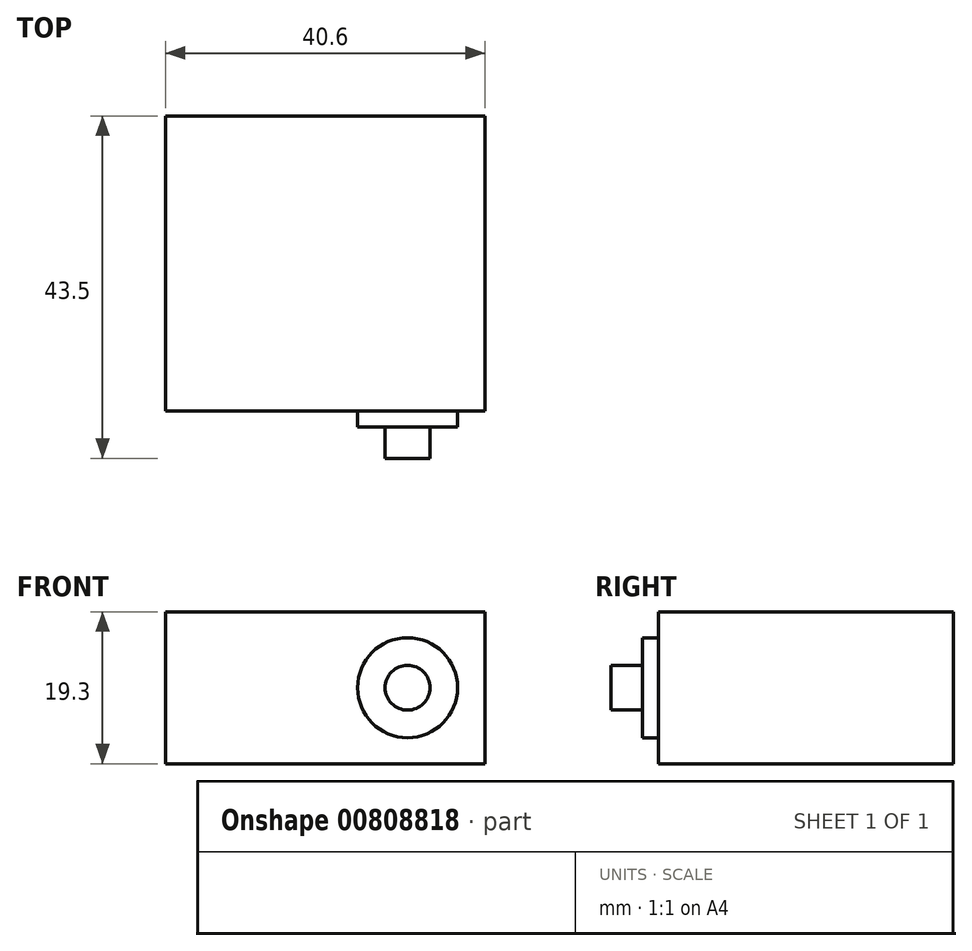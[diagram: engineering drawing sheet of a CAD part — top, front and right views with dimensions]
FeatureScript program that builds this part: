
annotation { "Feature Type Name" : "Feature", "Feature Type Description" : "" }
export const myFeature = defineFeature(function(context is Context, id is Id, definition is map)
    precondition{}
    {
        {
            var Q0;
            Q0=qCreatedBy(makeId("Front.planeOp"),FACE);
            var sketch = newSketch(context, id + "F0", { "sketchPlane" : qUnion([Q0])});
            skLineSegment(sketch, "E0.bottom", {"start": v(-20.3, 9.65) * mm, "end": v(20.3, 9.65) * mm});
            skLineSegment(sketch, "E0.top", {"start": v(-20.3, -9.65) * mm, "end": v(20.3, -9.65) * mm});
            skLineSegment(sketch, "E0.left", {"start": v(-20.3, 9.65) * mm, "end": v(-20.3, -9.65) * mm});
            skLineSegment(sketch, "E0.right", {"start": v(20.3, 9.65) * mm, "end": v(20.3, -9.65) * mm});
            skPoint(sketch, "E0.middle", {"position": v(0, 0) * mm});
            skSolve(sketch);
        }
        {
            var Q0;
            Q0=qSketchRegion(id+"F0",true);
            extrude(context, id + "F1", {"entities" : qUnion([Q0]), "depth" : 37.5 * mm, "offsetDistance" : 25 * mm});
        }
        {
            var Q0;
            Q0=makeQuery(id+"F1.opExtrude","CAP_FACE",FACE,{"disambiguationData":[OSD([sQuery(id+"F0.wireOp",EDGE,"E0.bottom"),sQuery(id+"F0.wireOp",EDGE,"E0.top"),sQuery(id+"F0.wireOp",EDGE,"E0.left"),sQuery(id+"F0.wireOp",EDGE,"E0.right")])],"isStart":false});
            var sketch = newSketch(context, id + "F2", { "sketchPlane" : qUnion([Q0])});
            skCircle(sketch, "E1", {"center": v(10.45, 0) * mm, "radius": 6.35 * mm});
            skSolve(sketch);
        }
        {
            var Q0;
            Q0=qSketchRegion(id+"F2",true);
            extrude(context, id + "F3", {"entities" : qUnion([Q0]), "operationType" : NewBodyOperationType.ADD, "depth" : 2 * mm, "offsetDistance" : 25 * mm});
        }
        {
            var Q0;
            Q0=makeQuery(id+"F3.opExtrude","CAP_FACE",FACE,{"disambiguationData":[OSD([sQuery(id+"F2.wireOp",EDGE,"E1")])],"isStart":false});
            var sketch = newSketch(context, id + "F4", { "sketchPlane" : qUnion([Q0])});
            skCircle(sketch, "E2", {"center": v(10.45, 0) * mm, "radius": 2.85 * mm});
            skSolve(sketch);
        }
        {
            var Q0;
            Q0=qSketchRegion(id+"F4",true);
            extrude(context, id + "F5", {"entities" : qUnion([Q0]), "operationType" : NewBodyOperationType.ADD, "depth" : 4 * mm, "offsetDistance" : 25 * mm});
        }
    });
